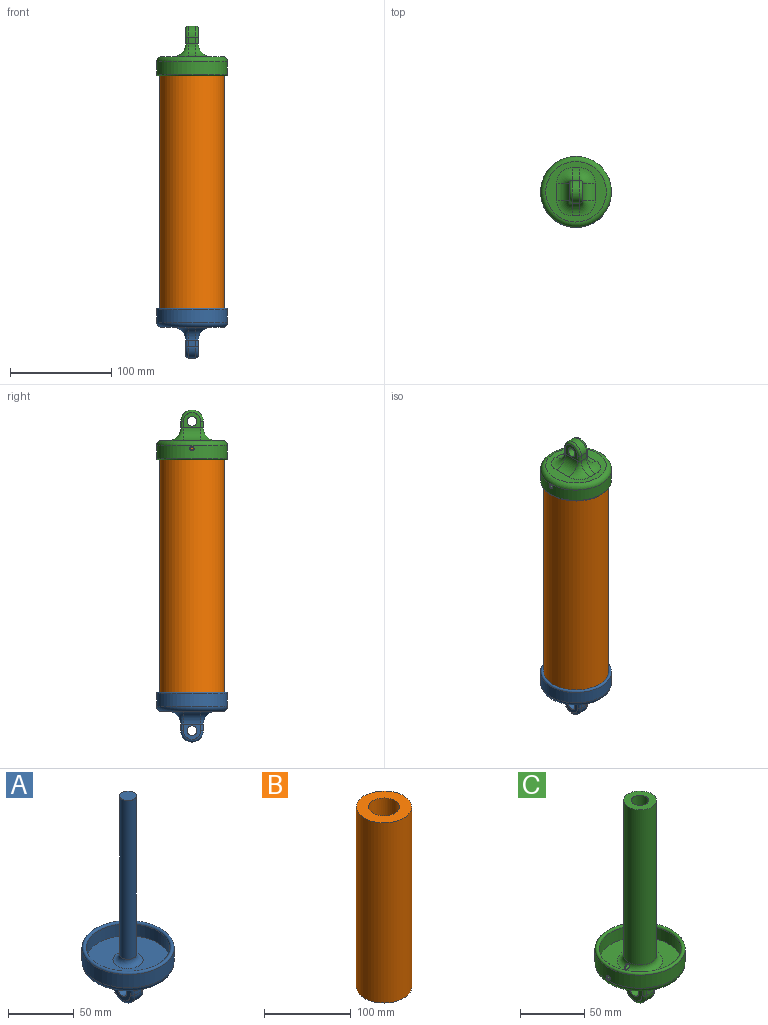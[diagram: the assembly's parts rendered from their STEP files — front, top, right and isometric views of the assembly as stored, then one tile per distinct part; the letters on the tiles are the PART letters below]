
ASSEMBLY  parts=3 mates=2
PART A: 29 faces, bbox 75.6x75.6x189.8 mm
  f0: plane 59.69x59.69mm, normal (0,0,-1), area 1183.2mm2, adj f14,f15,f16,f17,f18,f19,f20,f21
  f1: cylinder r=34.92mm len=69.85mm, axis (0,0,1), area 2717.2mm2, adj f22,f28
  f2: plane 7.62x6.35mm, normal (0,-1,0), area 48.4mm2, adj f3,f10,f13,f17
  f3: cylinder r=11.11mm len=22.23mm, axis (-1,0,0), area 266mm2, adj f2,f4,f9,f12
  f4: plane 7.62x6.35mm, normal (0,1,0), area 48.4mm2, adj f3,f8,f11,f18
  f5: cylinder r=4.76mm len=12.7mm, axis (-1,0,0), area 380mm2, adj f6,f7
  f6: plane 17.15x14.92mm, normal (1,0,0), area 153mm2, adj f5,f11,f12,f13,f14
  f7: plane 17.15x14.92mm, normal (-1,0,0), area 153mm2, adj f5,f8,f9,f10,f21
  f8: cylinder r=2.54mm len=6.35mm, axis (0,0,1), area 25.3mm2, adj f4,f7,f9,f20
  f9: torus R=8.57mm, axis (1,0,0), area 127.7mm2, adj f3,f7,f8,f10
  f10: cylinder r=2.54mm len=6.35mm, axis (0,0,-1), area 25.3mm2, adj f2,f7,f9,f19
  f11: cylinder r=2.54mm len=6.35mm, axis (0,0,-1), area 25.3mm2, adj f4,f6,f12,f16
  f12: torus R=8.57mm, axis (1,0,0), area 127.7mm2, adj f3,f6,f11,f13
  f13: cylinder r=2.54mm len=6.35mm, axis (0,0,1), area 25.3mm2, adj f2,f6,f12,f15
  f14: cylinder r=12.7mm len=17.15mm, axis (0,1,0), area 342mm2, adj f0,f6,f15,f16
  f15: torus R=15.24mm, axis (0,0,1), area 224.2mm2, adj f0,f13,f14,f17
  f16: torus R=15.24mm, axis (0,0,1), area 224.2mm2, adj f0,f11,f14,f18
  f17: cylinder r=12.7mm len=12.7mm, axis (1,0,0), area 152mm2, adj f0,f2,f15,f19
  f18: cylinder r=12.7mm len=12.7mm, axis (1,0,0), area 152mm2, adj f0,f4,f16,f20
  f19: torus R=15.24mm, axis (0,0,1), area 224.2mm2, adj f0,f10,f17,f21
  f20: torus R=15.24mm, axis (0,0,1), area 224.2mm2, adj f0,f8,f18,f21
  f21: cylinder r=12.7mm len=17.15mm, axis (0,-1,0), area 342mm2, adj f0,f7,f19,f20
  f22: torus R=29.84mm, axis (0,0,1), area 1658.5mm2, adj f0,f1
  f23: cylinder r=31.75mm len=63.5mm, axis (0,0,-1), area 2216.8mm2, adj f27,f28
  f24: plane 12.7x12.7mm, normal (0,0,1), area 126.7mm2, adj f25
  f25: cylinder r=6.35mm len=147.32mm, axis (0,0,-1), area 5877.8mm2, adj f24,f26
  f26: torus R=11.43mm, axis (0,0,1), area 410.9mm2, adj f25,f27
  f27: plane 63.5x63.5mm, normal (0,0,1), area 2756.5mm2, adj f23,f26
  f28: torus R=33.34mm, axis (0,0,1), area 1044.7mm2, adj f1,f23
PART B: 4 faces, bbox 63.5x63.5x254 mm
  f0: cylinder r=17.78mm len=254mm, axis (0,0,-1), area 28375.6mm2, adj f2,f3
  f1: cylinder r=31.75mm len=254mm, axis (0,0,-1), area 50670.7mm2, adj f2,f3
  f2: plane 63.5x63.5mm, normal (0,0,1), area 2173.8mm2, adj f0,f1
  f3: plane 63.5x63.5mm, normal (0,0,-1), area 2173.8mm2, adj f0,f1
PART C: 38 faces, bbox 75.7x75.7x189.9 mm
  f0: plane 63.55x63.55mm, normal (0,0,1), area 2173.8mm2, adj f5,f6,f34,f36
  f1: cylinder r=6.75mm len=152.4mm, axis (0,0,-1), area 6455.5mm2, adj f3,f4,f32
  f2: cylinder r=12.7mm len=147.32mm, axis (0,0,-1), area 11755.6mm2, adj f3,f5
  f3: plane 25.4x25.4mm, normal (0,0,1), area 363.6mm2, adj f1,f2
  f4: plane 13.5x13.5mm, normal (0,0,1), area 143.1mm2, adj f1
  f5: torus R=17.78mm, axis (0,0,1), area 709.8mm2, adj f0,f2,f33
  f6: cylinder r=31.75mm len=63.5mm, axis (0,0,-1), area 2204.2mm2, adj f0,f30,f35
  f7: torus R=8.57mm, axis (1,0,0), area 127.7mm2, adj f8,f12,f13,f14
  f8: cylinder r=11.11mm len=22.23mm, axis (-1,0,0), area 266mm2, adj f7,f10,f11,f15
  f9: cylinder r=4.76mm len=12.7mm, axis (-1,0,0), area 380mm2, adj f13,f17
  f10: torus R=8.57mm, axis (1,0,0), area 127.7mm2, adj f8,f16,f17,f18
  f11: plane 7.62x6.35mm, normal (0,1,0), area 48.4mm2, adj f8,f12,f18,f19
  f12: cylinder r=2.54mm len=6.35mm, axis (0,0,-1), area 25.3mm2, adj f7,f11,f13,f20
  f13: plane 17.15x14.92mm, normal (1,0,0), area 153mm2, adj f7,f9,f12,f14,f21
  f14: cylinder r=2.54mm len=6.35mm, axis (0,0,1), area 25.3mm2, adj f7,f13,f15,f22
  f15: plane 7.62x6.35mm, normal (0,-1,0), area 48.4mm2, adj f8,f14,f16,f23
  f16: cylinder r=2.54mm len=6.35mm, axis (0,0,-1), area 25.3mm2, adj f10,f15,f17,f24
  f17: plane 17.15x14.92mm, normal (-1,0,0), area 153mm2, adj f9,f10,f16,f18,f25
  f18: cylinder r=2.54mm len=6.35mm, axis (0,0,1), area 25.3mm2, adj f10,f11,f17,f26
  f19: cylinder r=12.7mm len=12.7mm, axis (1,0,0), area 152mm2, adj f11,f20,f26,f27
  f20: torus R=15.24mm, axis (0,0,1), area 224.2mm2, adj f12,f19,f21,f27
  f21: cylinder r=12.7mm len=17.15mm, axis (0,1,0), area 342mm2, adj f13,f20,f22,f27
  f22: torus R=15.24mm, axis (0,0,1), area 224.2mm2, adj f14,f21,f23,f27
  f23: cylinder r=12.7mm len=12.7mm, axis (1,0,0), area 152mm2, adj f15,f22,f24,f27
  f24: torus R=15.24mm, axis (0,0,1), area 224.2mm2, adj f16,f23,f25,f27
  f25: cylinder r=12.7mm len=17.15mm, axis (0,-1,0), area 342mm2, adj f17,f24,f26,f27
  f26: torus R=15.24mm, axis (0,0,1), area 224.2mm2, adj f18,f19,f25,f27
  f27: plane 59.69x59.69mm, normal (0,0,-1), area 1183.2mm2, adj f19,f20,f21,f22,f23,f24,f25,f26
  f28: torus R=29.84mm, axis (0,0,1), area 1658.5mm2, adj f27,f29
  f29: cylinder r=34.92mm len=69.85mm, axis (0,0,1), area 2703.2mm2, adj f28,f30,f37
  f30: torus R=33.34mm, axis (0,0,1), area 1044.7mm2, adj f6,f29
  f31: cylinder r=1.59mm len=3.18mm, axis (1,0,0), area 22mm2, adj f34,f35,f36,f37
  f32: cylinder r=1.59mm len=11.22mm, axis (1,0,0), area 72.6mm2, adj f1,f33
  f33: bspline ~5.41x4.32mm, area 9.8mm2, adj f5,f32
  f34: bspline ~1.45x0.57mm, area 0.4mm2, adj f0,f31,f35
  f35: bspline ~4.13x3.95mm, area 6.7mm2, adj f6,f31,f34,f36
  f36: bspline ~1.45x0.57mm, area 0.4mm2, adj f0,f31,f35
  f37: bspline ~4.26x4.19mm, area 9.1mm2, adj f29,f31
PLACE A at identity
PLACE B t=(0,0,127)mm
PLACE C rot(axis=(1,0,0),180deg) t=(0,0,254.33)mm
MATE fastened B.f1 <-> A.f1  axis (0,0,-1) through (0,0,0)mm
MATE slider C.f1 <-> A.f25  axis (0,0,-1) through (0,0,101.93)mm
